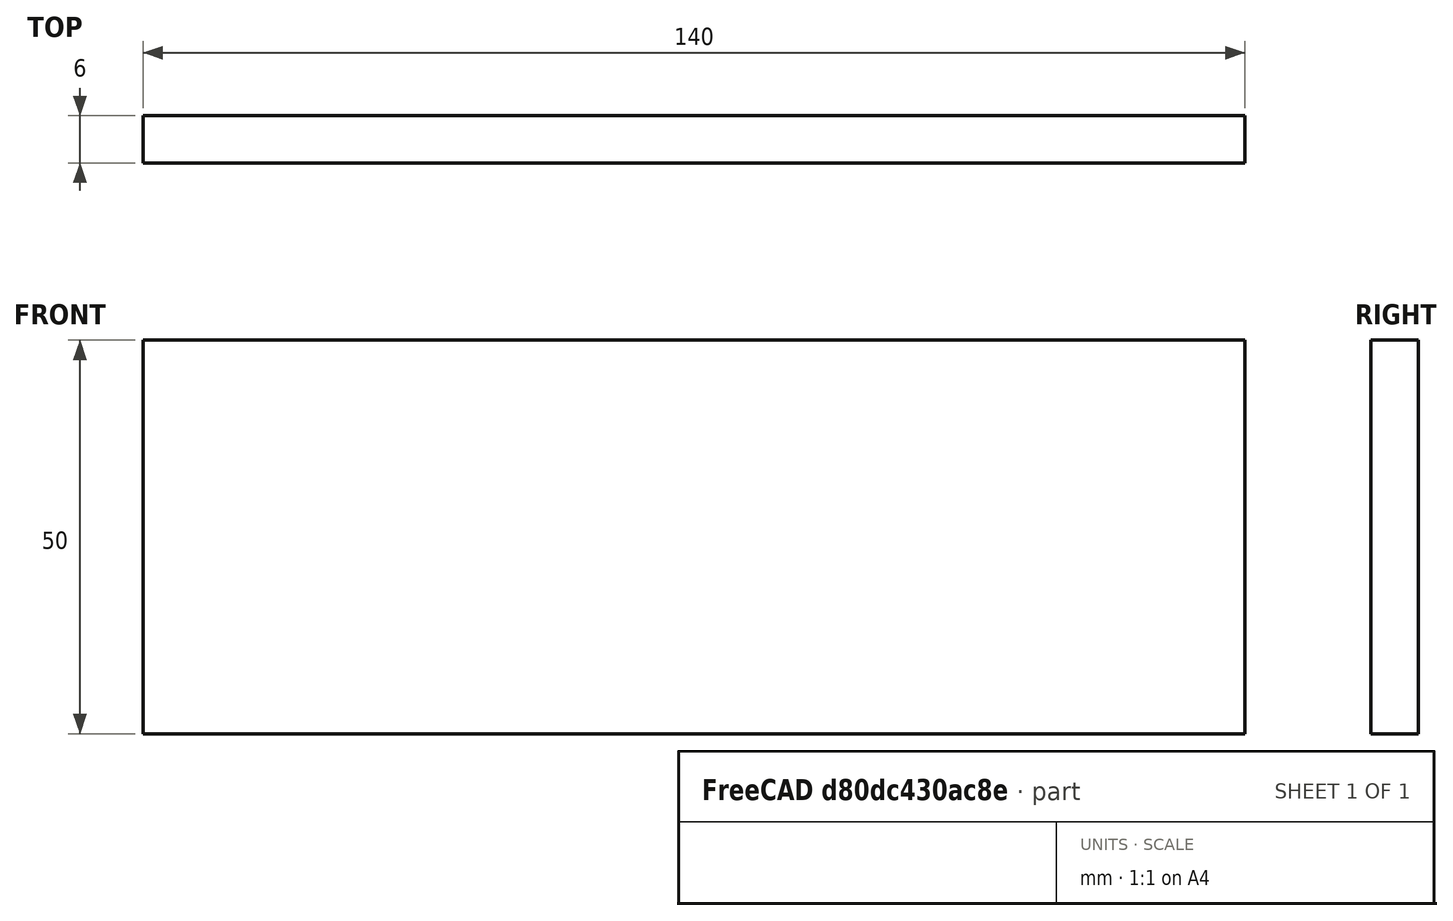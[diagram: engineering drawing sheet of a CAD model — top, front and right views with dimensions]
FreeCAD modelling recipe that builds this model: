
FCSTD DOCUMENT  (FreeCAD 0.15R4671 (Git))
Label: Flat Bar 140x6 EN10058 S235JR
License: All rights reserved
LicenseURL: http://en.wikipedia.org/wiki/All_rights_reserved
objects: Sketcher::SketchObject×1, Part::Extrusion×1
note: 2 computed .brp shape members not serialized (recipe doc carries the construction recipe); baked Part::Feature solids carry a one-line shape summary decoded from their .brp

FEATURE [Sketcher::SketchObject] Sketch
  sketch-geometry (4):
    g0: LineSegment StartX=-70 StartY=-3 StartZ=0 EndX=70 EndY=-3 EndZ=0
    g1: LineSegment StartX=70 StartY=-3 StartZ=0 EndX=70 EndY=3 EndZ=0
    g2: LineSegment StartX=70 StartY=3 StartZ=0 EndX=-70 EndY=3 EndZ=0
    g3: LineSegment StartX=-70 StartY=3 StartZ=0 EndX=-70 EndY=-3 EndZ=0
  constraints (12):
    c: Coincident(g0,g1)
    c: Coincident(g1,g2)
    c: Coincident(g2,g3)
    c: Coincident(g3,g0)
    c: Horizontal(g0)
    c: Horizontal(g2)
    c: Vertical(g1)
    c: Vertical(g3)
    c: Symmetric(g1,g2,g-2)
    c: Symmetric(g0,g1,g-1)
    c: DistanceY(g1) = 6
    c: DistanceX(g0) = 140
FEATURE [Part::Extrusion] Extrude  label="Flat Bar 140x6 EN10058 S235JR"
  Base = -> Sketch
  Dir = (0,0,50)
  Solid = true
